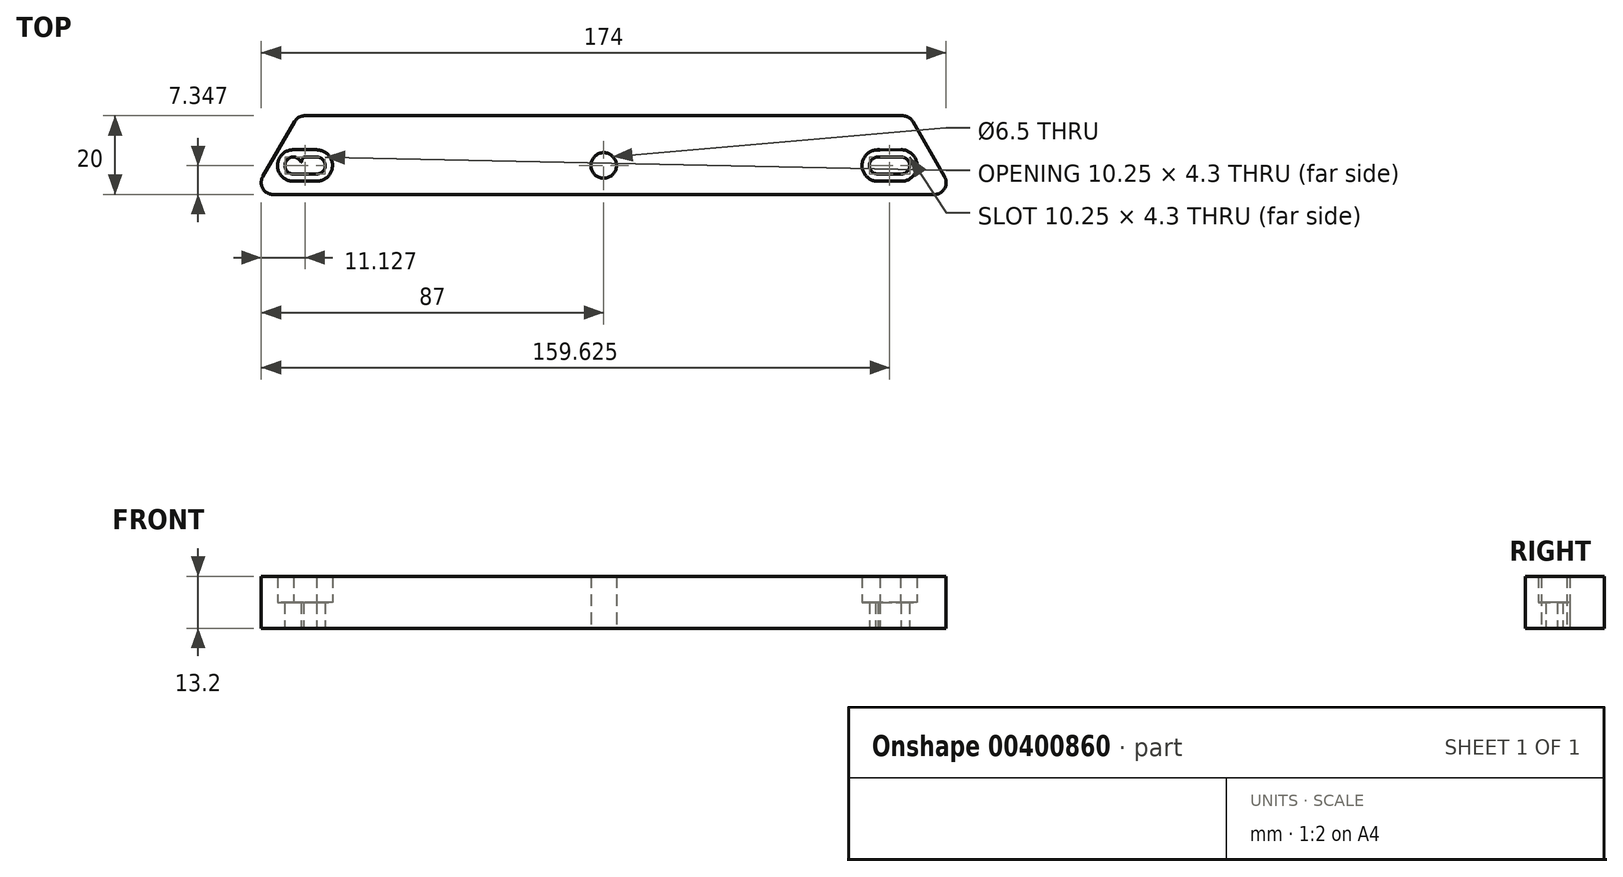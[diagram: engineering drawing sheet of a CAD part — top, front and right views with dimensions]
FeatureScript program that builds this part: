
annotation { "Feature Type Name" : "Feature", "Feature Type Description" : "" }
export const myFeature = defineFeature(function(context is Context, id is Id, definition is map)
    precondition{}
    {
        {
            var Q0;
            Q0=qCreatedBy(makeId("Top.planeOp"),FACE);
            var sketch = newSketch(context, id + "F0", { "sketchPlane" : qUnion([Q0])});
            skLineSegment(sketch, "E0", {"start": v(-89.2, -69.21) * mm, "end": v(89.2, -69.21) * mm});
            skLineSegment(sketch, "E1", {"start": v(89.2, -69.21) * mm, "end": v(0, 85.29) * mm});
            skLineSegment(sketch, "E2", {"start": v(0, 85.29) * mm, "end": v(-89.2, -69.21) * mm});
            skCircle(sketch, "E3", {"center": v(0, -61.86) * mm, "radius": 3.25 * mm});
            skCircle(sketch, "E4", {"center": v(-78.85, -61.86) * mm, "radius": 2.15 * mm});
            skCircle(sketch, "E5", {"center": v(-72.9, -61.86) * mm, "radius": 2.15 * mm});
            skCircle(sketch, "E6", {"center": v(69.65, -61.86) * mm, "radius": 2.15 * mm});
            skCircle(sketch, "E7", {"center": v(75.6, -61.86) * mm, "radius": 2.15 * mm});
            skLineSegment(sketch, "E8", {"start": v(-77.65, -49.21) * mm, "end": v(77.65, -49.21) * mm});
            skLineSegment(sketch, "E9", {"start": v(-78.96, -59.72) * mm, "end": v(-72.9, -59.71) * mm});
            skLineSegment(sketch, "E10", {"start": v(-72.83, -64.01) * mm, "end": v(-78.85, -64.01) * mm});
            skLineSegment(sketch, "E11", {"start": v(69.56, -59.72) * mm, "end": v(75.6, -59.71) * mm});
            skLineSegment(sketch, "E12", {"start": v(75.66, -64.01) * mm, "end": v(69.65, -64.01) * mm});
            skCircle(sketch, "E13", {"center": v(-78.85, -61.86) * mm, "radius": 4 * mm});
            skCircle(sketch, "E14", {"center": v(-72.9, -61.86) * mm, "radius": 4 * mm});
            skCircle(sketch, "E15", {"center": v(69.65, -61.86) * mm, "radius": 4 * mm});
            skCircle(sketch, "E16", {"center": v(75.6, -61.86) * mm, "radius": 4 * mm});
            skLineSegment(sketch, "E17", {"start": v(69.04, -57.91) * mm, "end": v(75.6, -57.86) * mm});
            skLineSegment(sketch, "E18", {"start": v(75.74, -65.86) * mm, "end": v(69.65, -65.86) * mm});
            skLineSegment(sketch, "E19", {"start": v(-78.96, -57.86) * mm, "end": v(-72.9, -57.86) * mm});
            skLineSegment(sketch, "E20", {"start": v(-72.83, -65.86) * mm, "end": v(-78.85, -65.86) * mm});
            skSolve(sketch);
        }
        {
            var Q0;
            {var subQ1=sQuery(id+"F0.wireOp",EDGE,"E0");Q0=makeQuery(id+"F0.imprint","IMPRINT",FACE,{"disambiguationData":[TD([[makeQuery(id+"F0.imprint","IMPRINT",EDGE,{"derivedFrom":subQ1}),1.0]])]});}
            extrude(context, id + "F1", {"entities" : qUnion([Q0]), "depth" : 6.6 * 2 * mm});
        }
        {
            var Q0;
            Q0=makeQuery(id+"F1.opExtrude","SWEPT_EDGE",EDGE,{"disambiguationData":[OSD([sQuery(id+"F0.wireOp",EDGE,"E0"),sQuery(id+"F0.wireOp",EDGE,"E2")])]});
            var Q1;
            Q1=makeQuery(id+"F1.opExtrude","SWEPT_EDGE",EDGE,{"disambiguationData":[OSD([sQuery(id+"F0.wireOp",EDGE,"E2"),sQuery(id+"F0.wireOp",EDGE,"E8")])]});
            var Q2;
            Q2=makeQuery(id+"F1.opExtrude","SWEPT_EDGE",EDGE,{"disambiguationData":[OSD([sQuery(id+"F0.wireOp",EDGE,"E0"),sQuery(id+"F0.wireOp",EDGE,"E1")])]});
            var Q3;
            Q3=makeQuery(id+"F1.opExtrude","SWEPT_EDGE",EDGE,{"disambiguationData":[OSD([sQuery(id+"F0.wireOp",EDGE,"E1"),sQuery(id+"F0.wireOp",EDGE,"E8")])]});
            fillet(context, id + "F2", {"entities" : qUnion([Q0, Q1, Q2, Q3]), "radius" : 3 * mm, "tangentPropagation" : true, "allowEdgeOverflow" : false});
        }
        {
            var Q0;
            {var subQ0=sQuery(id+"F0.wireOp",EDGE,"E14");var subQ1=sQuery(id+"F0.wireOp",EDGE,"E10");var subQ2=makeQuery(id+"F0.imprint","INTERSECT",VERTEX,{"derivedFrom":[subQ1,subQ0]});Q0=makeQuery(id+"F0.imprint","IMPRINT",FACE,{"disambiguationData":[TD([[makeQuery(id+"F0.imprint","IMPRINT",EDGE,{"disambiguationData":[TD([[subQ2,-1.0]])],"derivedFrom":subQ1}),1.0]])]});}
            var Q1;
            {var subQ0=sQuery(id+"F0.wireOp",EDGE,"E9");var subQ1=sQuery(id+"F0.wireOp",EDGE,"E4");var subQ5=makeQuery(id+"F0.imprint","INTERSECT",VERTEX,{"disambiguationData":[OD(0.0)],"derivedFrom":[subQ1,subQ0]});Q1=makeQuery(id+"F0.imprint","IMPRINT",FACE,{"disambiguationData":[TD([[makeQuery(id+"F0.imprint","IMPRINT",EDGE,{"disambiguationData":[TD([[subQ5,1.0]])],"derivedFrom":subQ1}),-1.0]])]});}
            var Q2;
            {var subQ0=sQuery(id+"F0.wireOp",EDGE,"E13");var subQ1=sQuery(id+"F0.wireOp",EDGE,"E9");var subQ2=makeQuery(id+"F0.imprint","INTERSECT",VERTEX,{"derivedFrom":[subQ1,subQ0]});Q2=makeQuery(id+"F0.imprint","IMPRINT",FACE,{"disambiguationData":[TD([[makeQuery(id+"F0.imprint","IMPRINT",EDGE,{"disambiguationData":[TD([[subQ2,-1.0]])],"derivedFrom":subQ1}),1.0]])]});}
            var Q3;
            {var subQ3=sQuery(id+"F0.wireOp",EDGE,"E16");var subQ10=makeQuery(id+"F0.imprint","IMPRINT",VERTEX,{"derivedFrom":subQ3});Q3=makeQuery(id+"F0.imprint","IMPRINT",FACE,{"disambiguationData":[TD([[makeQuery(id+"F0.imprint","IMPRINT",EDGE,{"disambiguationData":[TD([[subQ10,-1.0]])],"derivedFrom":subQ3}),1.0]])]});}
            var Q4;
            {var subQ0=sQuery(id+"F0.wireOp",EDGE,"E15");var subQ1=sQuery(id+"F0.wireOp",EDGE,"E11");var subQ2=makeQuery(id+"F0.imprint","INTERSECT",VERTEX,{"derivedFrom":[subQ1,subQ0]});Q4=makeQuery(id+"F0.imprint","IMPRINT",FACE,{"disambiguationData":[TD([[makeQuery(id+"F0.imprint","IMPRINT",EDGE,{"disambiguationData":[TD([[subQ2,-1.0]])],"derivedFrom":subQ1}),1.0]])]});}
            var Q5;
            {var subQ3=sQuery(id+"F0.wireOp",EDGE,"E15");var subQ12=makeQuery(id+"F0.imprint","IMPRINT",VERTEX,{"derivedFrom":subQ3});Q5=makeQuery(id+"F0.imprint","IMPRINT",FACE,{"disambiguationData":[TD([[makeQuery(id+"F0.imprint","IMPRINT",EDGE,{"disambiguationData":[TD([[subQ12,1.0]])],"derivedFrom":subQ3}),1.0]])]});}
            var Q6;
            {var subQ0=sQuery(id+"F0.wireOp",EDGE,"E16");var subQ1=sQuery(id+"F0.wireOp",EDGE,"E12");var subQ2=makeQuery(id+"F0.imprint","INTERSECT",VERTEX,{"derivedFrom":[subQ1,subQ0]});Q6=makeQuery(id+"F0.imprint","IMPRINT",FACE,{"disambiguationData":[TD([[makeQuery(id+"F0.imprint","IMPRINT",EDGE,{"disambiguationData":[TD([[subQ2,-1.0]])],"derivedFrom":subQ1}),1.0]])]});}
            var Q7;
            {var subQ0=sQuery(id+"F0.wireOp",EDGE,"E16");var subQ1=sQuery(id+"F0.wireOp",EDGE,"E11");var subQ2=makeQuery(id+"F0.imprint","INTERSECT",VERTEX,{"derivedFrom":[subQ1,subQ0]});Q7=makeQuery(id+"F0.imprint","IMPRINT",FACE,{"disambiguationData":[TD([[makeQuery(id+"F0.imprint","IMPRINT",EDGE,{"disambiguationData":[TD([[subQ2,-1.0]])],"derivedFrom":subQ1}),1.0]])]});}
            var Q8;
            {var subQ0=sQuery(id+"F0.wireOp",EDGE,"E16");var subQ1=sQuery(id+"F0.wireOp",EDGE,"E15");var subQ2=makeQuery(id+"F0.imprint","INTERSECT",VERTEX,{"disambiguationData":[OD(0.0)],"derivedFrom":[subQ1,subQ0]});Q8=makeQuery(id+"F0.imprint","IMPRINT",FACE,{"disambiguationData":[TD([[makeQuery(id+"F0.imprint","IMPRINT",EDGE,{"disambiguationData":[TD([[subQ2,-1.0]])],"derivedFrom":subQ1}),-1.0]])]});}
            var Q9;
            {var subQ0=sQuery(id+"F0.wireOp",EDGE,"E18");var subQ1=sQuery(id+"F0.wireOp",EDGE,"E15");var subQ2=makeQuery(id+"F0.imprint","INTERSECT",VERTEX,{"derivedFrom":[subQ1,subQ0]});Q9=makeQuery(id+"F0.imprint","IMPRINT",FACE,{"disambiguationData":[TD([[makeQuery(id+"F0.imprint","IMPRINT",EDGE,{"disambiguationData":[TD([[subQ2,-1.0]])],"derivedFrom":subQ1}),-1.0]])]});}
            var Q10;
            {var subQ0=sQuery(id+"F0.wireOp",EDGE,"E15");var subQ1=sQuery(id+"F0.wireOp",EDGE,"E12");var subQ2=makeQuery(id+"F0.imprint","INTERSECT",VERTEX,{"derivedFrom":[subQ1,subQ0]});Q10=makeQuery(id+"F0.imprint","IMPRINT",FACE,{"disambiguationData":[TD([[makeQuery(id+"F0.imprint","IMPRINT",EDGE,{"disambiguationData":[TD([[subQ2,-1.0]])],"derivedFrom":subQ1}),1.0]])]});}
            var Q11;
            {var subQ0=sQuery(id+"F0.wireOp",EDGE,"E13");var subQ1=sQuery(id+"F0.wireOp",EDGE,"E10");var subQ2=makeQuery(id+"F0.imprint","INTERSECT",VERTEX,{"derivedFrom":[subQ1,subQ0]});Q11=makeQuery(id+"F0.imprint","IMPRINT",FACE,{"disambiguationData":[TD([[makeQuery(id+"F0.imprint","IMPRINT",EDGE,{"disambiguationData":[TD([[subQ2,-1.0]])],"derivedFrom":subQ1}),1.0]])]});}
            var Q12;
            {var subQ0=sQuery(id+"F0.wireOp",EDGE,"E20");var subQ1=sQuery(id+"F0.wireOp",EDGE,"E13");var subQ2=makeQuery(id+"F0.imprint","INTERSECT",VERTEX,{"derivedFrom":[subQ1,subQ0]});Q12=makeQuery(id+"F0.imprint","IMPRINT",FACE,{"disambiguationData":[TD([[makeQuery(id+"F0.imprint","IMPRINT",EDGE,{"disambiguationData":[TD([[subQ2,-1.0]])],"derivedFrom":subQ1}),-1.0]])]});}
            var Q13;
            {var subQ0=sQuery(id+"F0.wireOp",EDGE,"E14");var subQ1=sQuery(id+"F0.wireOp",EDGE,"E9");var subQ2=makeQuery(id+"F0.imprint","INTERSECT",VERTEX,{"derivedFrom":[subQ1,subQ0]});Q13=makeQuery(id+"F0.imprint","IMPRINT",FACE,{"disambiguationData":[TD([[makeQuery(id+"F0.imprint","IMPRINT",EDGE,{"disambiguationData":[TD([[subQ2,-1.0]])],"derivedFrom":subQ1}),1.0]])]});}
            var Q14;
            {var subQ0=sQuery(id+"F0.wireOp",EDGE,"E14");var subQ1=sQuery(id+"F0.wireOp",EDGE,"E13");var subQ2=makeQuery(id+"F0.imprint","INTERSECT",VERTEX,{"disambiguationData":[OD(0.0)],"derivedFrom":[subQ1,subQ0]});Q14=makeQuery(id+"F0.imprint","IMPRINT",FACE,{"disambiguationData":[TD([[makeQuery(id+"F0.imprint","IMPRINT",EDGE,{"disambiguationData":[TD([[subQ2,-1.0]])],"derivedFrom":subQ1}),-1.0]])]});}
            extrude(context, id + "F3", {"entities" : qUnion([Q0, Q1, Q2, Q3, Q4, Q5, Q6, Q7, Q8, Q9, Q10, Q11, Q12, Q13, Q14]), "operationType" : NewBodyOperationType.ADD, "depth" : 6.6 * mm});
        }
    });
